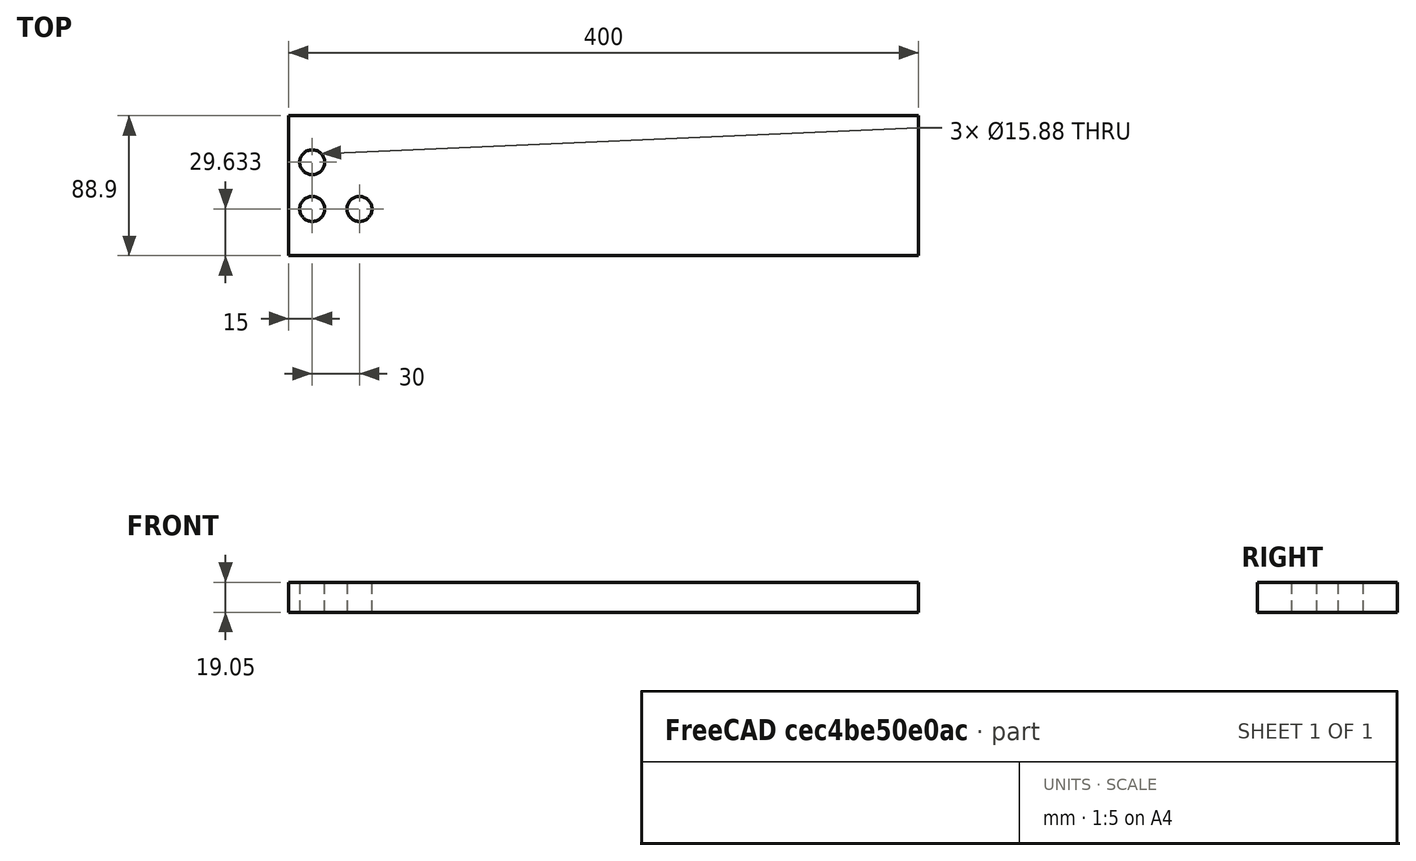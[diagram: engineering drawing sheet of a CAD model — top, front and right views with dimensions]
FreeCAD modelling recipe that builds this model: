
FCSTD DOCUMENT  (FreeCAD 0.19R24291 (Git))
Label: top
License: All rights reserved
LicenseURL: http://en.wikipedia.org/wiki/All_rights_reserved
objects: Sketcher::SketchObject×1, PartDesign::Pad×1, PartDesign::Body×1
note: 4 computed .brp shape members not serialized (recipe doc carries the construction recipe); baked Part::Feature solids carry a one-line shape summary decoded from their .brp

FEATURE [Sketcher::SketchObject] Sketch
  FullyConstrained = true
  MapMode = 5
  Support = -> [XY_Plane]
  expr: Constraints[24] = 3.5 * 25.4 * 1 / 3
  expr: Constraints[15] = 3.5 * 25.4 / 3
  sketch-geometry (9):
    g0: LineSegment StartX=0 StartY=0 StartZ=0 EndX=400 EndY=0 EndZ=0
    g1: LineSegment StartX=400 StartY=0 StartZ=0 EndX=400 EndY=88.9 EndZ=0
    g2: LineSegment StartX=400 StartY=88.9 StartZ=0 EndX=0 EndY=88.9 EndZ=0
    g3: LineSegment StartX=0 StartY=88.9 StartZ=0 EndX=0 EndY=0 EndZ=0
    g4: Circle CenterX=15 CenterY=29.6333 CenterZ=0 NormalX=0 NormalY=0 NormalZ=1 AngleXU=0 Radius=7.9375
    g5: LineSegment StartX=0 StartY=29.6333 StartZ=0 EndX=400 EndY=29.6333 EndZ=0
    g6: Circle CenterX=45 CenterY=29.6333 CenterZ=0 NormalX=0 NormalY=0 NormalZ=1 AngleXU=0 Radius=7.9375
    g7: LineSegment StartX=0 StartY=59.2667 StartZ=0 EndX=400 EndY=59.2667 EndZ=0
    g8: Circle CenterX=15 CenterY=59.2667 CenterZ=0 NormalX=0 NormalY=0 NormalZ=1 AngleXU=0 Radius=7.9375
  constraints (28):
    c: Coincident(g0,g1)
    c: Coincident(g1,g2)
    c: Coincident(g2,g3)
    c: Coincident(g3,g0)
    c: Horizontal(g0)
    c: Horizontal(g2)
    c: Vertical(g1)
    c: Vertical(g3)
    c: Coincident(g0,g-1)
    c: Diameter(g4) = 15.875
    c: DistanceY(g3,g3) = 88.9
    c: DistanceX(g0,g0) = 400
    c: PointOnObject(g5,g3)
    c: PointOnObject(g5,g1)
    c: Horizontal(g5)
    c: DistanceY(g0,g5) = 29.6333
    c: PointOnObject(g4,g5)
    c: DistanceX(g5,g4) = 15
    c: Equal(g4,g6) = 15.875
    c: PointOnObject(g6,g5)
    c: DistanceX(g4,g6) = 30
    c: Parallel(g0,g7)
    c: PointOnObject(g7,g3)
    c: PointOnObject(g7,g1)
    c: DistanceY(g5,g7) = 29.6333
    c: Equal(g4,g8) = 15.875
    c: PointOnObject(g8,g7)
    c: Vertical(g4,g8)
FEATURE [PartDesign::Pad] Pad
  Direction = (1,1,1)
  Length = 19.05
  Length2 = 100
  Profile = -> Sketch
  Type = 0
FEATURE [PartDesign::Body] Body
  Group = -> [Sketch,Pad]
  Origin = -> Origin
  Tip = -> Pad
